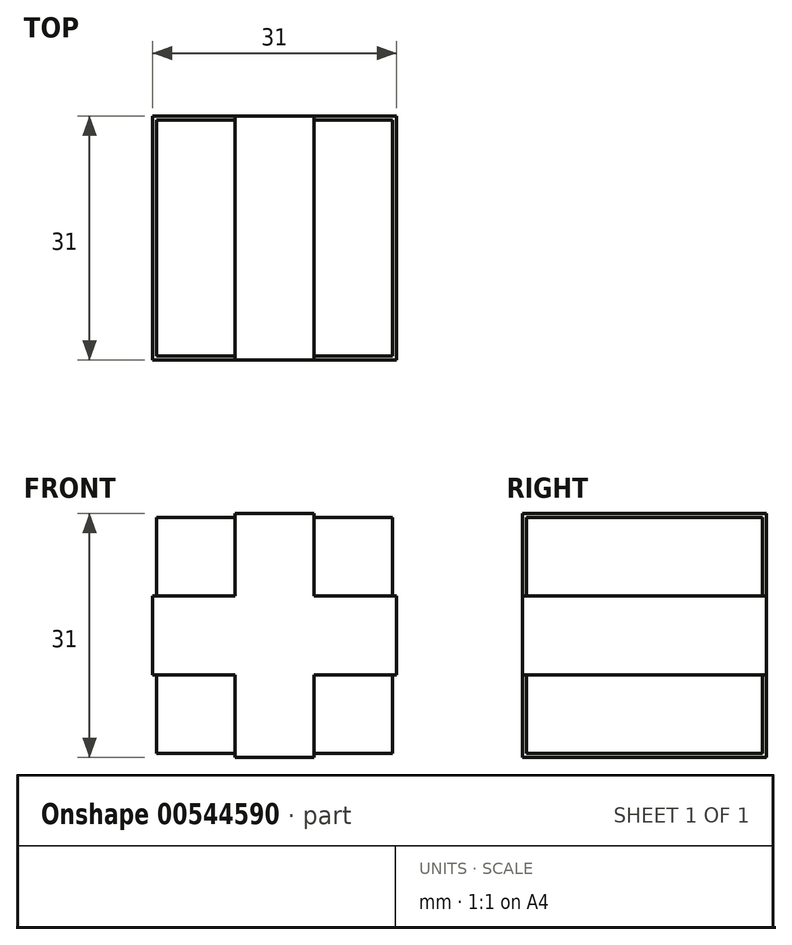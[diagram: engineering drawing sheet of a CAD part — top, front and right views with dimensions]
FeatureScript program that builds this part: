
annotation { "Feature Type Name" : "Feature", "Feature Type Description" : "" }
export const myFeature = defineFeature(function(context is Context, id is Id, definition is map)
    precondition{}
    {
        {
            var Q0;
            Q0=qCreatedBy(makeId("Top.planeOp"),FACE);
            var sketch = newSketch(context, id + "F0", { "sketchPlane" : qUnion([Q0])});
            skLineSegment(sketch, "E0.bottom", {"start": v(0, 0) * mm, "end": v(30, 0) * mm});
            skLineSegment(sketch, "E0.top", {"start": v(0, -30) * mm, "end": v(30, -30) * mm});
            skLineSegment(sketch, "E0.left", {"start": v(0, 0) * mm, "end": v(0, -30) * mm});
            skLineSegment(sketch, "E0.right", {"start": v(30, 0) * mm, "end": v(30, -30) * mm});
            skSolve(sketch);
        }
        {
            var Q0;
            Q0 = qSketchRegion(id + "F0", true);
            extrude(context, id + "F1", {"entities" : qUnion([Q0]), "depth" : 30 * mm, "offsetDistance" : 25 * mm});
        }
        {
            var Q0;
            Q0=makeQuery(id+"F1.opExtrude","CAP_FACE",FACE,{"disambiguationData":[OSD([sQuery(id+"F0.wireOp",EDGE,"E0.bottom"),sQuery(id+"F0.wireOp",EDGE,"E0.top"),sQuery(id+"F0.wireOp",EDGE,"E0.left"),sQuery(id+"F0.wireOp",EDGE,"E0.right")])],"isStart":false});
            var sketch = newSketch(context, id + "F2", { "sketchPlane" : qUnion([Q0])});
            skLineSegment(sketch, "E1", {"start": v(0, 0) * mm, "end": v(10, 0) * mm});
            skLineSegment(sketch, "E2", {"start": v(10, 0) * mm, "end": v(10, -30) * mm});
            skLineSegment(sketch, "E3", {"start": v(10, -30) * mm, "end": v(20, -30) * mm});
            skLineSegment(sketch, "E4", {"start": v(20, -30) * mm, "end": v(20, 0) * mm});
            skLineSegment(sketch, "E5", {"start": v(20, 0) * mm, "end": v(10, 0) * mm});
            skSolve(sketch);
        }
        {
            var Q0;
            Q0 = qSketchRegion(id + "F2", true);
            extrude(context, id + "F3", {"entities" : qUnion([Q0]), "operationType" : NewBodyOperationType.ADD, "depth" : 0.5 * mm, "offsetDistance" : 25 * mm});
        }
        {
            var Q0;
            Q0=makeQuery(id+"F1.opExtrude","SWEPT_FACE",FACE,{"disambiguationData":[OSD([sQuery(id+"F0.wireOp",EDGE,"E0.left")])]});
            var sketch = newSketch(context, id + "F4", { "sketchPlane" : qUnion([Q0])});
            skLineSegment(sketch, "E6", {"start": v(0, 0) * mm, "end": v(0, 10) * mm});
            skLineSegment(sketch, "E7", {"start": v(0, 10) * mm, "end": v(0, 20) * mm});
            skLineSegment(sketch, "E8", {"start": v(0, 20) * mm, "end": v(30, 20) * mm});
            skLineSegment(sketch, "E9", {"start": v(30, 20) * mm, "end": v(30, 10) * mm});
            skLineSegment(sketch, "E10", {"start": v(30, 10) * mm, "end": v(0, 10) * mm});
            skSolve(sketch);
        }
        {
            var Q0;
            Q0 = qSketchRegion(id + "F4", true);
            extrude(context, id + "F5", {"entities" : qUnion([Q0]), "operationType" : NewBodyOperationType.ADD, "depth" : 0.5 * mm, "offsetDistance" : 25 * mm});
        }
        {
            var Q0;
            Q0=makeQuery(id+"F1.opExtrude","SWEPT_FACE",FACE,{"disambiguationData":[OSD([sQuery(id+"F0.wireOp",EDGE,"E0.right")])]});
            var sketch = newSketch(context, id + "F6", { "sketchPlane" : qUnion([Q0])});
            skLineSegment(sketch, "E11", {"start": v(0, 0) * mm, "end": v(0, 10) * mm});
            skLineSegment(sketch, "E12", {"start": v(0, 10) * mm, "end": v(0, 20) * mm});
            skLineSegment(sketch, "E13", {"start": v(0, 20) * mm, "end": v(-30, 20) * mm});
            skLineSegment(sketch, "E14", {"start": v(-30, 20) * mm, "end": v(-30, 10) * mm});
            skLineSegment(sketch, "E15", {"start": v(-30, 10) * mm, "end": v(0, 10) * mm});
            skSolve(sketch);
        }
        {
            var Q0;
            Q0 = qSketchRegion(id + "F6", true);
            extrude(context, id + "F7", {"entities" : qUnion([Q0]), "operationType" : NewBodyOperationType.ADD, "depth" : 0.5 * mm, "offsetDistance" : 25 * mm});
        }
        {
            var Q0;
            Q0=makeQuery(id+"F1.opExtrude","CAP_FACE",FACE,{"disambiguationData":[OSD([sQuery(id+"F0.wireOp",EDGE,"E0.bottom"),sQuery(id+"F0.wireOp",EDGE,"E0.top"),sQuery(id+"F0.wireOp",EDGE,"E0.left"),sQuery(id+"F0.wireOp",EDGE,"E0.right")])],"isStart":true});
            var sketch = newSketch(context, id + "F8", { "sketchPlane" : qUnion([Q0])});
            skLineSegment(sketch, "E16", {"start": v(0, 0) * mm, "end": v(10, 0) * mm});
            skLineSegment(sketch, "E17", {"start": v(10, 0) * mm, "end": v(20, 0) * mm});
            skLineSegment(sketch, "E18", {"start": v(20, 0) * mm, "end": v(20, 30) * mm});
            skLineSegment(sketch, "E19", {"start": v(20, 30) * mm, "end": v(10, 30) * mm});
            skLineSegment(sketch, "E20", {"start": v(10, 30) * mm, "end": v(10, 0) * mm});
            skSolve(sketch);
        }
        {
            var Q0;
            Q0 = qSketchRegion(id + "F8", true);
            extrude(context, id + "F9", {"entities" : qUnion([Q0]), "operationType" : NewBodyOperationType.ADD, "depth" : 0.5 * mm, "offsetDistance" : 25 * mm});
        }
        {
            var Q0;
            Q0=makeQuery(id+"F9.boolean.opBoolean","MERGE",FACE,{"derivedFrom":[makeQuery(id+"F7.boolean.opBoolean","MERGE",FACE,{"derivedFrom":[makeQuery(id+"F5.boolean.opBoolean","MERGE",FACE,{"derivedFrom":[makeQuery(id+"F3.boolean.opBoolean","MERGE",FACE,{"derivedFrom":[makeQuery(id+"F1.opExtrude","SWEPT_FACE",FACE,{"disambiguationData":[OSD([sQuery(id+"F0.wireOp",EDGE,"E0.top")])]}),makeQuery(id+"F3.opExtrude","SWEPT_FACE",FACE,{"disambiguationData":[OSD([sQuery(id+"F2.wireOp",EDGE,"E3")])]})]}),makeQuery(id+"F5.opExtrude","SWEPT_FACE",FACE,{"disambiguationData":[OSD([sQuery(id+"F4.wireOp",EDGE,"E9")])]})]}),makeQuery(id+"F7.opExtrude","SWEPT_FACE",FACE,{"disambiguationData":[OSD([sQuery(id+"F6.wireOp",EDGE,"E14")])]})]}),makeQuery(id+"F9.opExtrude","SWEPT_FACE",FACE,{"disambiguationData":[OSD([sQuery(id+"F8.wireOp",EDGE,"E19")])]})]});
            var sketch = newSketch(context, id + "F10", { "sketchPlane" : qUnion([Q0])});
            skLineSegment(sketch, "E21", {"start": v(20, -0.5) * mm, "end": v(20, 10) * mm});
            skLineSegment(sketch, "E22", {"start": v(20, 30.5) * mm, "end": v(10, 30.5) * mm});
            skLineSegment(sketch, "E23", {"start": v(10, 30.5) * mm, "end": v(10, 20) * mm});
            skLineSegment(sketch, "E24", {"start": v(-0.5, 20) * mm, "end": v(10, 20) * mm});
            skLineSegment(sketch, "E25", {"start": v(30.5, 20) * mm, "end": v(30.5, 10) * mm});
            skLineSegment(sketch, "E26", {"start": v(30.5, 10) * mm, "end": v(20, 10) * mm});
            skLineSegment(sketch, "E27", {"start": v(-0.5, 10) * mm, "end": v(-0.5, 20) * mm});
            skLineSegment(sketch, "E28.trimOffspring", {"start": v(10, 10) * mm, "end": v(10, -0.5) * mm});
            skLineSegment(sketch, "E29.trimOffspring", {"start": v(20, 20) * mm, "end": v(30.5, 20) * mm});
            skLineSegment(sketch, "E30.trimOffspring", {"start": v(20, 20) * mm, "end": v(20, 30.5) * mm});
            skLineSegment(sketch, "E31.trimOffspring", {"start": v(10, 10) * mm, "end": v(-0.5, 10) * mm});
            skSolve(sketch);
        }
        {
            var Q0;
            {var subQ24=sQuery(id+"F10.wireOp",EDGE,"E22");Q0=makeQuery(id+"F10.imprint","IMPRINT",FACE,{"disambiguationData":[TD([[makeQuery(id+"F10.imprint","IMPRINT",EDGE,{"derivedFrom":subQ24}),-1.0]])]});}
            extrude(context, id + "F11", {"entities" : qUnion([Q0]), "operationType" : NewBodyOperationType.ADD, "depth" : 0.5 * mm, "offsetDistance" : 25 * mm});
        }
        {
            var Q0;
            Q0=makeQuery(id+"F9.boolean.opBoolean","MERGE",FACE,{"derivedFrom":[makeQuery(id+"F7.boolean.opBoolean","MERGE",FACE,{"derivedFrom":[makeQuery(id+"F5.boolean.opBoolean","MERGE",FACE,{"derivedFrom":[makeQuery(id+"F3.boolean.opBoolean","MERGE",FACE,{"derivedFrom":[makeQuery(id+"F1.opExtrude","SWEPT_FACE",FACE,{"disambiguationData":[OSD([sQuery(id+"F0.wireOp",EDGE,"E0.bottom")])]}),makeQuery(id+"F3.opExtrude","SWEPT_FACE",FACE,{"disambiguationData":[OSD([sQuery(id+"F2.wireOp",EDGE,"E5")])]})]}),makeQuery(id+"F5.opExtrude","SWEPT_FACE",FACE,{"disambiguationData":[OSD([sQuery(id+"F4.wireOp",EDGE,"E7")])]})]}),makeQuery(id+"F7.opExtrude","SWEPT_FACE",FACE,{"disambiguationData":[OSD([sQuery(id+"F6.wireOp",EDGE,"E12")])]})]}),makeQuery(id+"F9.opExtrude","SWEPT_FACE",FACE,{"disambiguationData":[OSD([sQuery(id+"F8.wireOp",EDGE,"E17")])]})]});
            var sketch = newSketch(context, id + "F12", { "sketchPlane" : qUnion([Q0])});
            skPoint(sketch, "E32.endSnap0", {"position": v(-5, 0) * mm});
            skLineSegment(sketch, "E33", {"start": v(-20, -0.5) * mm, "end": v(-10, -0.5) * mm});
            skLineSegment(sketch, "E34", {"start": v(-10, -0.5) * mm, "end": v(-10, 10) * mm});
            skLineSegment(sketch, "E35", {"start": v(-10, 30.5) * mm, "end": v(-20, 30.5) * mm});
            skLineSegment(sketch, "E36", {"start": v(-20, 30.5) * mm, "end": v(-20, 20) * mm});
            skLineSegment(sketch, "E37", {"start": v(-30.5, 10) * mm, "end": v(-20, 10) * mm});
            skLineSegment(sketch, "E38", {"start": v(0.5, 10) * mm, "end": v(0.5, 20) * mm});
            skLineSegment(sketch, "E39", {"start": v(0.5, 20) * mm, "end": v(-10, 20) * mm});
            skLineSegment(sketch, "E40", {"start": v(-30.5, 20) * mm, "end": v(-30.5, 10) * mm});
            skLineSegment(sketch, "E41.trimOffspring", {"start": v(-20, 20) * mm, "end": v(-30.5, 20) * mm});
            skLineSegment(sketch, "E42.trimOffspring", {"start": v(-10, 20) * mm, "end": v(-10, 30.5) * mm});
            skLineSegment(sketch, "E43.trimOffspring", {"start": v(-20, 10) * mm, "end": v(-20, -0.5) * mm});
            skLineSegment(sketch, "E44.trimOffspring", {"start": v(-10, 10) * mm, "end": v(0.5, 10) * mm});
            skSolve(sketch);
        }
        {
            var Q0;
            Q0 = qSketchRegion(id + "F12", true);
            extrude(context, id + "F13", {"entities" : qUnion([Q0]), "operationType" : NewBodyOperationType.ADD, "depth" : 0.5 * mm, "offsetDistance" : 25 * mm});
        }
    });
